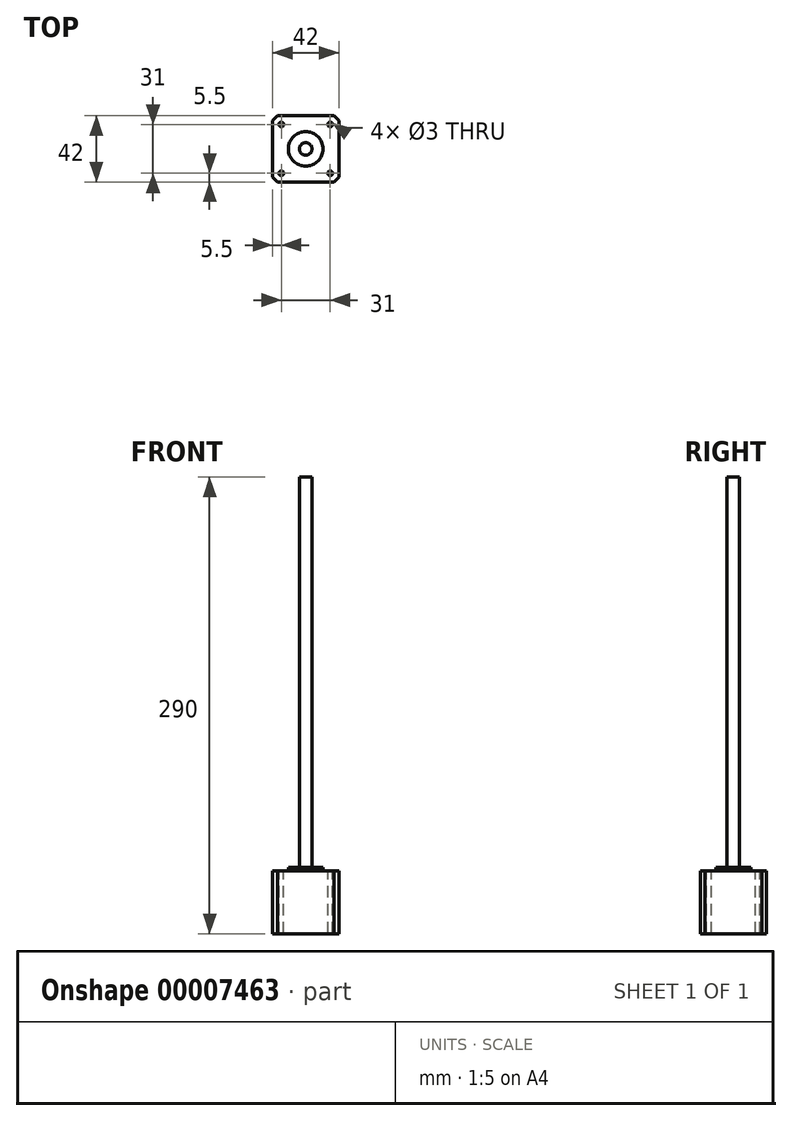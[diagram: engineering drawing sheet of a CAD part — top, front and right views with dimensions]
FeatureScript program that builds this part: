
annotation { "Feature Type Name" : "Feature", "Feature Type Description" : "" }
export const myFeature = defineFeature(function(context is Context, id is Id, definition is map)
    precondition{}
    {
        {
            var Q0;
            Q0=qCreatedBy(makeId("Top.planeOp"),FACE);
            var sketch = newSketch(context, id + "F0", { "sketchPlane" : qUnion([Q0])});
            skCircle(sketch, "E0", {"center": v(0, 0) * mm, "radius": 4 * mm});
            skCircle(sketch, "E1", {"center": v(0, 0) * mm, "radius": 11 * mm});
            skLineSegment(sketch, "E2.bottom", {"start": v(15.5, 15.5) * mm, "end": v(-15.5, 15.5) * mm, "construction": true});
            skLineSegment(sketch, "E2.top", {"start": v(15.5, -15.5) * mm, "end": v(-15.5, -15.5) * mm, "construction": true});
            skLineSegment(sketch, "E2.left", {"start": v(15.5, 15.5) * mm, "end": v(15.5, -15.5) * mm, "construction": true});
            skLineSegment(sketch, "E2.right", {"start": v(-15.5, 15.5) * mm, "end": v(-15.5, -15.5) * mm, "construction": true});
            skLineSegment(sketch, "E3.bottom", {"start": v(21, 21) * mm, "end": v(-21, 21) * mm, "construction": true});
            skLineSegment(sketch, "E3.top", {"start": v(21, -21) * mm, "end": v(-21, -21) * mm, "construction": true});
            skLineSegment(sketch, "E3.left", {"start": v(21, 21) * mm, "end": v(21, -21) * mm, "construction": true});
            skLineSegment(sketch, "E3.right", {"start": v(-21, 21) * mm, "end": v(-21, -21) * mm, "construction": true});
            skCircle(sketch, "E4", {"center": v(-15.5, 15.5) * mm, "radius": 1.5 * mm});
            skCircle(sketch, "E5", {"center": v(15.5, 15.5) * mm, "radius": 1.5 * mm});
            skCircle(sketch, "E6", {"center": v(15.5, -15.5) * mm, "radius": 1.5 * mm});
            skCircle(sketch, "E7", {"center": v(-15.5, -15.5) * mm, "radius": 1.5 * mm});
            skLineSegment(sketch, "E8", {"start": v(-18, 21) * mm, "end": v(18, 21) * mm});
            skLineSegment(sketch, "E9", {"start": v(18, 21) * mm, "end": v(21, 18) * mm});
            skLineSegment(sketch, "E10", {"start": v(21, 18) * mm, "end": v(21, -18) * mm});
            skLineSegment(sketch, "E11", {"start": v(21, -18) * mm, "end": v(18, -21) * mm});
            skLineSegment(sketch, "E12", {"start": v(18, -21) * mm, "end": v(-18, -21) * mm});
            skLineSegment(sketch, "E13", {"start": v(-18, -21) * mm, "end": v(-21, -18) * mm});
            skLineSegment(sketch, "E14", {"start": v(-21, -18) * mm, "end": v(-21, 18) * mm});
            skLineSegment(sketch, "E15", {"start": v(-21, 18) * mm, "end": v(-18, 21) * mm});
            skLineSegment(sketch, "E16", {"start": v(-21, 18) * mm, "end": v(21, 18) * mm, "construction": true});
            skLineSegment(sketch, "E17", {"start": v(-21, -18) * mm, "end": v(21, -18) * mm, "construction": true});
            skLineSegment(sketch, "E18", {"start": v(-18, 21) * mm, "end": v(-18, -21) * mm, "construction": true});
            skLineSegment(sketch, "E19", {"start": v(18, -21) * mm, "end": v(18, 21) * mm, "construction": true});
            skSolve(sketch);
        }
        {
            var Q0;
            Q0=makeQuery(id+"F0.imprint","IMPRINT",FACE,{"disambiguationData":[TD([[makeQuery(id+"F0.imprint","IMPRINT",EDGE,{"derivedFrom":sQuery(id+"F0.wireOp",EDGE,"E1")}),-1.0]])]});
            var Q1;
            Q1=makeQuery(id+"F0.imprint","IMPRINT",FACE,{"disambiguationData":[TD([[makeQuery(id+"F0.imprint","IMPRINT",EDGE,{"derivedFrom":sQuery(id+"F0.wireOp",EDGE,"E0")}),-1.0]])]});
            var Q2;
            Q2=makeQuery(id+"F0.imprint","IMPRINT",FACE,{"disambiguationData":[TD([[makeQuery(id+"F0.imprint","IMPRINT",EDGE,{"derivedFrom":sQuery(id+"F0.wireOp",EDGE,"E0")}),1.0]])]});
            extrude(context, id + "F1", {"entities" : qUnion([Q0, Q1, Q2]), "oppositeDirection" : true, "depth" : 40 * mm});
        }
        {
            var Q0;
            Q0=makeQuery(id+"F0.imprint","IMPRINT",FACE,{"disambiguationData":[TD([[makeQuery(id+"F0.imprint","IMPRINT",EDGE,{"derivedFrom":sQuery(id+"F0.wireOp",EDGE,"E0")}),-1.0]])]});
            extrude(context, id + "F2", {"entities" : qUnion([Q0]), "operationType" : NewBodyOperationType.ADD, "depth" : 2 * mm});
        }
        {
            var Q0;
            Q0=makeQuery(id+"F0.imprint","IMPRINT",FACE,{"disambiguationData":[TD([[makeQuery(id+"F0.imprint","IMPRINT",EDGE,{"derivedFrom":sQuery(id+"F0.wireOp",EDGE,"E0")}),1.0]])]});
            extrude(context, id + "F3", {"entities" : qUnion([Q0]), "operationType" : NewBodyOperationType.ADD, "depth" : 250 * mm});
        }
    });
